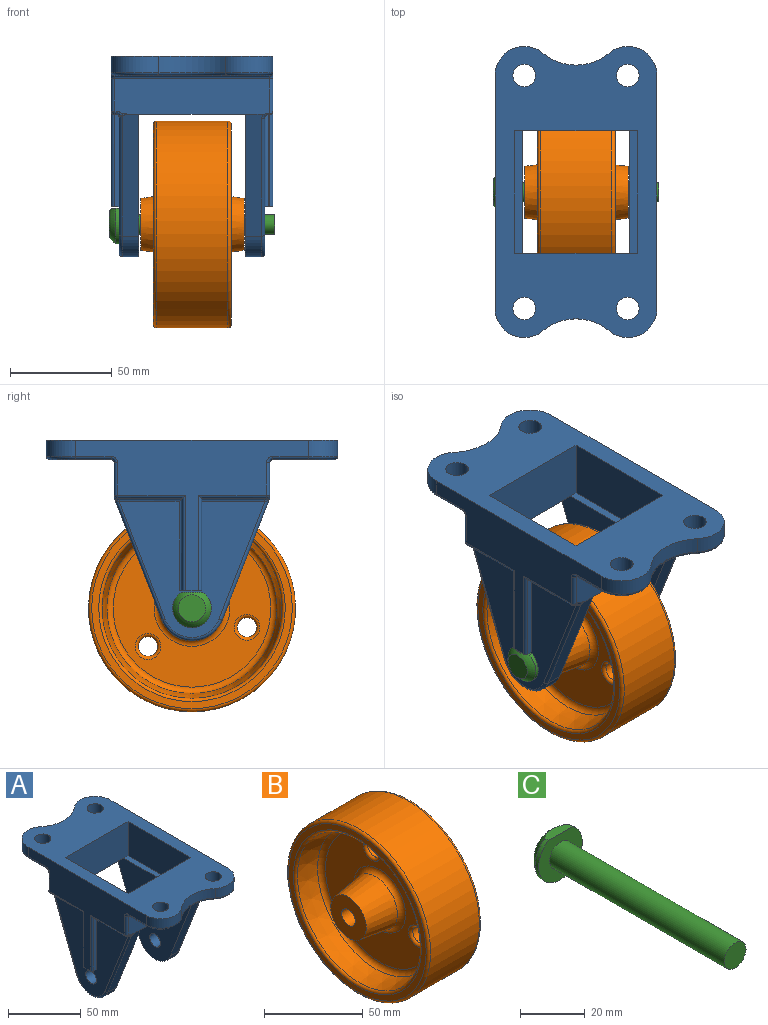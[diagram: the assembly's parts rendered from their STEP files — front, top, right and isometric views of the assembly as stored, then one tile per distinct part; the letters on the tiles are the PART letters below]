
ASSEMBLY  parts=3 mates=2
PART A: 103 faces, bbox 82.3x145.8x100.3 mm
  f0: plane 60.33x3.97mm, normal (0,0,1), area 239.4mm2, adj f6,f20,f21,f22
  f1: plane 31.75x0.87mm, normal (0,0,-1), area 25.2mm2, adj f45,f65,f66,f72,f100
  f2: plane 32.94x0.85mm, normal (0,0,-1), area 25.9mm2, adj f42,f49,f52,f57
  f3: plane 71.55x66.68mm, normal (-1,0,0), area 2433.3mm2, adj f8,f45,f46,f62,f63,f64,f65,f67
  f4: plane 71.55x66.68mm, normal (1,0,0), area 2364mm2, adj f35,f41,f50,f51,f52,f53,f58,f59
  f5: plane 76.2x70.15mm, normal (1,0,0), area 3293mm2, adj f7,f8,f9,f10,f31,f38,f39,f40
  f6: plane 76.17x69.85mm, normal (-1,0,0), area 3293mm2, adj f0,f34,f35,f36,f37,f39,f40,f74
  f7: plane 60.23x23.8mm, normal (0,0.93,-0.36), area 508.2mm2, adj f5,f10,f31,f64,f69,f89
  f8: cylinder r=5.16mm len=10.32mm, axis (-1,0,0), area 308.8mm2, adj f3,f5
  f9: plane 59.92x23.49mm, normal (0,-0.93,-0.36), area 508.2mm2, adj f5,f10,f32,f62,f66,f101
  f10: cylinder r=15.88mm len=29.58mm, axis (-1,0,0), area 302.1mm2, adj f5,f7,f9,f63
  f11: plane 31.75x0.87mm, normal (0,0,-1), area 25.2mm2, adj f44,f68,f69,f71,f87
  f12: plane 76.2x30.16mm, normal (0,0,-1), area 1770.8mm2, adj f23,f28,f77,f78,f79,f81,f82,f83
  f13: plane 114.3x73.82mm, normal (1,0,0), area 2600.1mm2, adj f14,f26,f29,f41,f47,f48,f49,f54
  f14: cylinder r=14.29mm len=23.43mm, axis (0,0,-1), area 256.9mm2, adj f13,f15,f29,f77
  f15: cylinder r=25.4mm len=32.51mm, axis (0,0,-1), area 280mm2, adj f14,f16,f29,f79
  f16: cylinder r=14.29mm len=23.43mm, axis (0,0,-1), area 256.9mm2, adj f15,f17,f29,f81
  f17: plane 114.3x73.82mm, normal (-1,0,0), area 2600.1mm2, adj f16,f18,f29,f46,f70,f71,f72,f73
  f18: cylinder r=14.29mm len=23.43mm, axis (0,0,-1), area 256.9mm2, adj f17,f19,f29,f93
  f19: cylinder r=25.4mm len=32.51mm, axis (0,0,-1), area 280mm2, adj f18,f26,f29,f91
  f20: plane 60.33x28.58mm, normal (0,-1,0), area 1723.8mm2, adj f0,f21,f27,f29,f38,f40
  f21: plane 60.33x28.58mm, normal (-1,0,0), area 1723.8mm2, adj f0,f20,f22,f29
  f22: plane 60.33x28.58mm, normal (0,1,0), area 1723.8mm2, adj f0,f21,f27,f29,f38,f39
  f23: cylinder r=5.56mm len=11.11mm, axis (0,0,-1), area 332.5mm2, adj f12,f29
  f24: cylinder r=5.56mm len=11.11mm, axis (0,0,-1), area 332.5mm2, adj f29,f30
  f25: cylinder r=5.56mm len=11.11mm, axis (0,0,-1), area 332.5mm2, adj f29,f30
  f26: cylinder r=14.29mm len=23.43mm, axis (0,0,-1), area 256.9mm2, adj f13,f19,f29,f90
  f27: plane 60.33x28.58mm, normal (1,0,0), area 1723.8mm2, adj f20,f22,f29,f38
  f28: cylinder r=5.56mm len=11.11mm, axis (0,0,-1), area 332.5mm2, adj f12,f29
  f29: plane 142.88x79.38mm, normal (0,0,1), area 6623.4mm2, adj f13,f14,f15,f16,f17,f18,f19,f20
  f30: plane 76.2x30.16mm, normal (0,0,-1), area 1770.8mm2, adj f24,f25,f90,f91,f92,f93,f95,f96
  f31: plane 76.2x17.47mm, normal (0,1,0), area 1302.9mm2, adj f5,f7,f54,f74,f76,f82,f85,f87
  f32: plane 76.74x18mm, normal (0,-1,0), area 1324.5mm2, adj f9,f37,f39,f48,f57,f96,f98,f100
  f33: plane 32.53x0.82mm, normal (0,0,-1), area 25.5mm2, adj f43,f51,f55,f76
  f34: plane 59.47x23.2mm, normal (0,0.93,-0.36), area 507.1mm2, adj f6,f36,f60,f61,f74
  f35: cylinder r=5.16mm len=10.32mm, axis (-1,0,0), area 308.8mm2, adj f4,f6
  f36: cylinder r=15.88mm len=29.58mm, axis (-1,0,0), area 302.1mm2, adj f6,f34,f37,f59
  f37: plane 59.75x23.31mm, normal (0,-0.93,-0.36), area 509.7mm2, adj f6,f32,f36,f57,f58
  f38: plane 60.33x3.97mm, normal (0,0,1), area 239.4mm2, adj f5,f20,f22,f27
  f39: plane 52.39x7.94mm, normal (0,0,-1), area 415.8mm2, adj f5,f6,f22,f32
  f40: plane 52.39x7.91mm, normal (0,0,-1), area 414.3mm2, adj f5,f6,f20,f74
  f41: plane 12.7x3.97mm, normal (0,0,-1), area 37.8mm2, adj f4,f13,f42,f43,f47,f50,f53,f56
  f42: plane 45.24x0.79mm, normal (0,-1,0), area 35.9mm2, adj f2,f41,f47,f53
  f43: plane 45.24x0.79mm, normal (0,1,0), area 35.9mm2, adj f33,f41,f50,f56
  f44: plane 45.24x0.79mm, normal (0,1,0), area 35.9mm2, adj f11,f46,f67,f70
  f45: plane 45.24x2.38mm, normal (0,-1,0), area 107.2mm2, adj f1,f3,f46,f65,f73
  f46: plane 11.11x3.97mm, normal (0,0,-1), area 37.3mm2, adj f3,f17,f44,f45,f67,f70,f73
  f47: cylinder r=1.59mm len=46.83mm, axis (0,0,-1), area 114.8mm2, adj f13,f41,f42,f49
  f48: cylinder r=1.59mm len=17.37mm, axis (0,0,-1), area 41.8mm2, adj f13,f32,f49,f57,f94
  f49: cylinder r=1.59mm len=34.83mm, axis (0,-1,0), area 82.8mm2, adj f2,f13,f47,f48,f57
  f50: cylinder r=1.59mm len=45.24mm, axis (0,0,-1), area 110.8mm2, adj f4,f41,f43,f51
  f51: cylinder r=1.59mm len=31.75mm, axis (0,1,0), area 76.8mm2, adj f4,f33,f50,f61,f76
  f52: cylinder r=1.59mm len=32.25mm, axis (0,1,0), area 76.9mm2, adj f2,f4,f53,f57
  f53: cylinder r=1.59mm len=45.24mm, axis (0,0,1), area 110.8mm2, adj f4,f41,f42,f52
  f54: cylinder r=1.59mm len=17.26mm, axis (0,0,1), area 41.3mm2, adj f13,f31,f55,f76,f80
  f55: cylinder r=1.59mm len=34.72mm, axis (0,-1,0), area 83.2mm2, adj f13,f33,f54,f56,f76
  f56: cylinder r=1.59mm len=46.83mm, axis (0,0,1), area 114.8mm2, adj f13,f41,f43,f55
  f57: bspline ~5.22x3.31mm, area 7.6mm2, adj f2,f32,f37,f48,f49,f52,f58
  f58: cylinder r=1.59mm len=58.16mm, axis (0,-0.36,0.93), area 154.1mm2, adj f4,f37,f57,f59
  f59: torus R=14.29mm, axis (1,0,0), area 91.5mm2, adj f4,f36,f58,f60
  f60: cylinder r=1.59mm len=58.16mm, axis (0,-0.36,-0.93), area 154.1mm2, adj f4,f34,f59,f61
  f61: bspline ~2.33x2.18mm, area 3.6mm2, adj f34,f51,f60,f75
  f62: cylinder r=1.59mm len=59.31mm, axis (0,0.36,-0.93), area 155.7mm2, adj f3,f9,f63,f66
  f63: torus R=14.29mm, axis (1,0,0), area 91.5mm2, adj f3,f10,f62,f64
  f64: cylinder r=1.59mm len=59.31mm, axis (0,0.36,0.93), area 155.7mm2, adj f3,f7,f63,f69
  f65: cylinder r=1.59mm len=31.01mm, axis (0,-1,0), area 77.3mm2, adj f1,f3,f45,f66
  f66: bspline ~4.13x4mm, area 3.5mm2, adj f1,f9,f62,f65,f102
  f67: cylinder r=1.59mm len=45.24mm, axis (0,0,1), area 110.8mm2, adj f3,f44,f46,f68
  f68: cylinder r=1.59mm len=31.01mm, axis (0,-1,0), area 75.4mm2, adj f3,f11,f67,f69
  f69: bspline ~3.78x3.41mm, area 3.5mm2, adj f7,f11,f64,f68,f88
  f70: cylinder r=1.59mm len=46.83mm, axis (0,0,-1), area 114.8mm2, adj f17,f44,f46,f71
  f71: cylinder r=1.59mm len=33.34mm, axis (0,-1,0), area 81.2mm2, adj f11,f17,f70,f86
  f72: cylinder r=1.59mm len=33.34mm, axis (0,-1,0), area 81.2mm2, adj f1,f17,f73,f99
  f73: cylinder r=1.59mm len=46.83mm, axis (0,0,1), area 114.8mm2, adj f17,f45,f46,f72
  f74: cylinder r=1.59mm len=60.95mm, axis (-1,0,0), area 20.8mm2, adj f5,f6,f31,f34,f40,f75
  f75: sphere r=1.59mm, area 0.7mm2, adj f61,f74,f76
  f76: torus R=3.17mm, axis (0,1,0), area 7.5mm2, adj f31,f33,f51,f54,f55,f75
  f77: torus R=12.7mm, axis (0,0,1), area 77.4mm2, adj f12,f14,f78,f79
  f78: cylinder r=1.59mm len=17.46mm, axis (0,1,0), area 43.5mm2, adj f12,f13,f77,f80
  f79: torus R=26.99mm, axis (0,0,1), area 90mm2, adj f12,f15,f77,f81
  f80: torus R=3.17mm, axis (-1,0,0), area 8.5mm2, adj f13,f54,f78,f82
  f81: torus R=12.7mm, axis (0,0,1), area 77.4mm2, adj f12,f16,f79,f83
  f82: cylinder r=1.59mm len=76.2mm, axis (1,0,0), area 190mm2, adj f12,f31,f80,f84
  f83: cylinder r=1.59mm len=17.46mm, axis (0,-1,0), area 43.5mm2, adj f12,f17,f81,f84
  f84: torus R=3.17mm, axis (-1,0,0), area 8.5mm2, adj f17,f82,f83,f85
  f85: cylinder r=1.59mm len=15.88mm, axis (0,0,-1), area 39.6mm2, adj f17,f31,f84,f86
  f86: sphere r=1.59mm, area 4mm2, adj f71,f85,f87
  f87: cylinder r=1.59mm len=1.59mm, axis (-1,0,0), area 2.2mm2, adj f11,f31,f86,f88
  f88: bspline ~4.27x2.32mm, area 6.2mm2, adj f31,f69,f87,f89
  f89: bspline ~2.31x1.05mm, area 0.7mm2, adj f7,f31,f88
  f90: torus R=12.7mm, axis (0,0,1), area 77.4mm2, adj f26,f30,f91,f92
  f91: torus R=26.99mm, axis (0,0,1), area 90mm2, adj f19,f30,f90,f93
  f92: cylinder r=1.59mm len=17.46mm, axis (0,1,0), area 43.5mm2, adj f13,f30,f90,f94
  f93: torus R=12.7mm, axis (0,0,1), area 77.4mm2, adj f18,f30,f91,f95
  f94: torus R=3.17mm, axis (-1,0,0), area 8.5mm2, adj f13,f48,f92,f96
  f95: cylinder r=1.59mm len=17.46mm, axis (0,-1,0), area 43.5mm2, adj f17,f30,f93,f97
  f96: cylinder r=1.59mm len=76.2mm, axis (-1,0,0), area 190mm2, adj f30,f32,f94,f97
  f97: torus R=3.17mm, axis (-1,0,0), area 8.5mm2, adj f17,f95,f96,f98
  f98: cylinder r=1.59mm len=15.88mm, axis (0,0,1), area 39.6mm2, adj f17,f32,f97,f99
  f99: sphere r=1.59mm, area 4mm2, adj f72,f98,f100
  f100: cylinder r=1.59mm len=1.59mm, axis (1,0,0), area 2.2mm2, adj f1,f32,f99,f102
  f101: bspline ~2.26x1.02mm, area 0.7mm2, adj f9,f32,f102
  f102: bspline ~4.27x2.32mm, area 6.2mm2, adj f32,f66,f100,f101
PART B: 26 faces, bbox 50.8x110x110 mm
  f0: plane 25.4x25.4mm, normal (1,0,0), area 433.5mm2, adj f1,f22
  f1: cone r=12.7mm half-angle=8.1deg, axis (-1,0,0), area 1744.1mm2, adj f0,f2
  f2: torus R=18.63mm, axis (1,0,0), area 476.6mm2, adj f1,f3
  f3: plane 77.34x77.34mm, normal (1,0,0), area 3394.4mm2, adj f2,f4,f19,f20,f21
  f4: torus R=38.67mm, axis (1,0,0), area 1110.5mm2, adj f3,f5
  f5: cone r=41.79mm half-angle=11.3deg, axis (1,0,0), area 3318.4mm2, adj f4,f6
  f6: torus R=45.75mm, axis (1,0,0), area 614mm2, adj f5,f7
  f7: plane 98.43x98.43mm, normal (1,0,0), area 1032.6mm2, adj f6,f8
  f8: torus R=49.21mm, axis (1,0,0), area 786.9mm2, adj f7,f9
  f9: cylinder r=50.8mm len=101.6mm, axis (1,0,0), area 11147.6mm2, adj f8,f10
  f10: torus R=49.21mm, axis (1,0,0), area 786.9mm2, adj f9,f11
  f11: plane 98.43x98.43mm, normal (-1,0,0), area 1032.6mm2, adj f10,f12
  f12: torus R=45.75mm, axis (1,0,0), area 614mm2, adj f11,f13
  f13: cone r=41.79mm half-angle=11.3deg, axis (-1,0,0), area 3318.4mm2, adj f12,f14
  f14: torus R=38.67mm, axis (1,0,0), area 1110.5mm2, adj f13,f15
  f15: plane 77.34x77.34mm, normal (-1,0,0), area 3228.1mm2, adj f14,f16,f23,f24,f25
  f16: torus R=18.63mm, axis (1,0,0), area 476.6mm2, adj f15,f17
  f17: cone r=12.7mm half-angle=8.1deg, axis (1,0,0), area 1744.1mm2, adj f16,f18
  f18: plane 25.4x25.4mm, normal (-1,0,0), area 433.5mm2, adj f17,f22
  f19: cylinder r=4.76mm len=9.53mm, axis (1,0,0), area 142.5mm2, adj f3,f25
  f20: cylinder r=4.76mm len=9.53mm, axis (1,0,0), area 142.5mm2, adj f3,f24
  f21: cylinder r=4.76mm len=9.53mm, axis (1,0,0), area 142.5mm2, adj f3,f23
  f22: cylinder r=4.83mm len=50.8mm, axis (1,0,0), area 1540.4mm2, adj f0,f18
  f23: torus R=6.35mm, axis (1,0,0), area 83.7mm2, adj f15,f21
  f24: torus R=6.35mm, axis (1,0,0), area 83.7mm2, adj f15,f20
  f25: torus R=6.35mm, axis (1,0,0), area 83.7mm2, adj f15,f19
PART C: 7 faces, bbox 19.1x81x19.1 mm
  f0: sphere r=11.11mm, area 202.8mm2, adj f2,f5,f6
  f1: plane 19.05x17.46mm, normal (0,-1,0), area 202.4mm2, adj f2,f3,f6
  f2: cylinder r=9.53mm len=19.05mm, axis (0,-1,0), area 77.1mm2, adj f0,f1,f6
  f3: cylinder r=4.76mm len=76.2mm, axis (0,1,0), area 2280.2mm2, adj f1,f4
  f4: plane 9.53x9.53mm, normal (0,-1,0), area 71.3mm2, adj f3
  f5: plane 13.3x13.3mm, normal (0,1,0), area 139mm2, adj f0
  f6: plane 10.53x3.64mm, normal (0,0,1), area 31.5mm2, adj f0,f1,f2
PLACE A t=(-1.27,-2.06,62.95)mm
PLACE B t=(-1.12,-2.06,8.98)mm
PLACE C rot(axis=(0,0,1),90deg) t=(-36.99,-2.06,8.98)mm
MATE cylindrical B.f1 <-> C.f2  axis (1,0,0) through (-7.02,-2.06,8.98)mm
MATE revolute C.f2 <-> A.f8  axis (1,0,0) through (-36.99,-2.06,8.98)mm
